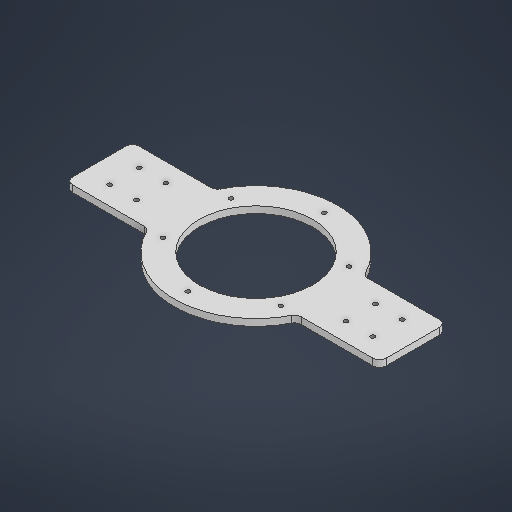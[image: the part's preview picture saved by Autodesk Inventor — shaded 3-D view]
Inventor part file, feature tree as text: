
AUTODESK INVENTOR PART (.ipt)
format: ipt  version: 2025 (Build 290162000, 162)  size: 268,288 bytes
history: native  units: in
note: dims shown in document units (in); Inventor stores cm internally (conversion verified against a paired STEP export)
features: sketch x4, hole x2, extrude x1, fillet x1
ambient origin geometry x8: Origin, YZ Plane, XZ Plane, XY Plane, X Axis, Y Axis, Z Axis, Center Point
bodies: Solid1 (feature_tree)
feature tree (8):
  extrude  "Extrusion1"  Depth=0.1969in TaperAngle=0.0deg
  hole  "Hole1"  [1 undecoded]
  hole  "Hole2"  [1 undecoded]
  fillet  "Fillet2"  Radius=2.3622in
  sketch  "Sketch1"  dims[d0=3.3465in d3=0.1969in d4=0.0in]
  sketch  "Sketch2"  dims[d33=4.0157in d34=0.1575in d35=2.3622in d37=360.0deg]
  sketch  "Sketch3"  dims[d39=0.1276in d40=0.315in d41=0.1575in d42=0.0787in d43=90.0deg d44=0.4646in d45=0.8108in d46=9.252in d47=1.9685in d51=0.1575in d52=0.748in d53=0.5512in d54=0.1575in d55=0.7874in d56=0.1969in]
  sketch  "Sketch Circular Pattern1"  dims[d11=0.1276in d12=0.315in d13=0.1575in d14=0.0787in d15=90.0deg d16=0.4646in d17=0.8108in d29=2.4016in]
note: 2 required parameter values undecoded (feature->parameter linkage not recoverable at this tier; creation-order binding heuristic only, values carry confidence <= 0.55)
